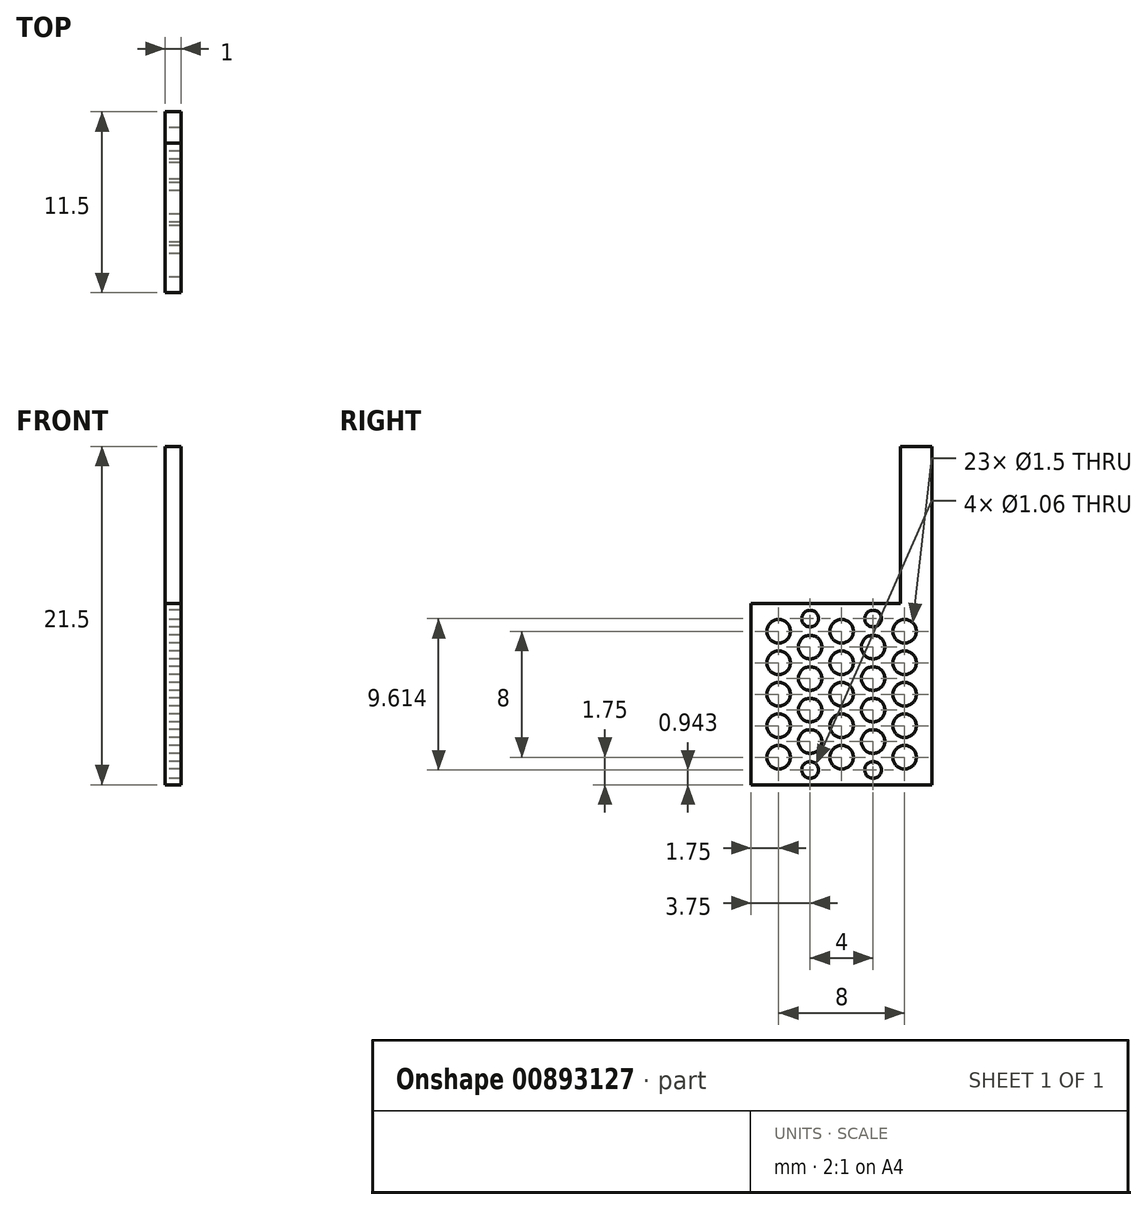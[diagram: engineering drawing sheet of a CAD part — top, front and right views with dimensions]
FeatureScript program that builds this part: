
annotation { "Feature Type Name" : "Feature", "Feature Type Description" : "" }
export const myFeature = defineFeature(function(context is Context, id is Id, definition is map)
    precondition{}
    {
        {
            var Q0;
            Q0=qCreatedBy(makeId("Right.planeOp"),FACE);
            var sketch = newSketch(context, id + "F0", { "sketchPlane" : qUnion([Q0])});
            skLineSegment(sketch, "E0.bottom", {"start": v(0, 0) * mm, "end": v(8.38, 0) * mm});
            skLineSegment(sketch, "E0.top", {"start": v(0, -11.5) * mm, "end": v(11.5, -11.5) * mm});
            skLineSegment(sketch, "E0.left", {"start": v(0, 0) * mm, "end": v(0, -11.5) * mm});
            skLineSegment(sketch, "E1", {"start": v(11.5, 0) * mm, "end": v(11.5, -11.5) * mm});
            skLineSegment(sketch, "E2", {"start": v(10.38, 10) * mm, "end": v(9.5, 10) * mm});
            skLineSegment(sketch, "E3.trimOffspring", {"start": v(10.38, 0) * mm, "end": v(11.5, 0) * mm});
            skCircle(sketch, "E4", {"center": v(1.75, -5.75) * mm, "radius": 0.75 * mm});
            skCircle(sketch, "E5.MirrorC", {"center": v(1.75, -1.75) * mm, "radius": 0.75 * mm});
            skCircle(sketch, "E6.MirrorC", {"center": v(1.75, -3.75) * mm, "radius": 0.75 * mm});
            skCircle(sketch, "E7.MirrorC", {"center": v(1.75, -9.75) * mm, "radius": 0.75 * mm});
            skCircle(sketch, "E8.MirrorC", {"center": v(1.75, -7.75) * mm, "radius": 0.75 * mm});
            skCircle(sketch, "E9", {"center": v(3.75, -2.75) * mm, "radius": 0.75 * mm});
            skCircle(sketch, "E10", {"center": v(3.75, -10.56) * mm, "radius": 0.53 * mm});
            skCircle(sketch, "E11.MirrorC", {"center": v(5.75, -1.75) * mm, "radius": 0.75 * mm});
            skCircle(sketch, "E12.MirrorC", {"center": v(5.75, -3.75) * mm, "radius": 0.75 * mm});
            skCircle(sketch, "E13.MirrorC", {"center": v(5.75, -5.75) * mm, "radius": 0.75 * mm});
            skCircle(sketch, "E14.MirrorC", {"center": v(5.75, -7.75) * mm, "radius": 0.75 * mm});
            skCircle(sketch, "E15.MirrorC", {"center": v(5.75, -9.75) * mm, "radius": 0.75 * mm});
            skCircle(sketch, "E16.MirrorC", {"center": v(7.75, -2.75) * mm, "radius": 0.75 * mm});
            skCircle(sketch, "E17.MirrorC", {"center": v(9.75, -1.75) * mm, "radius": 0.75 * mm});
            skCircle(sketch, "E18.MirrorC", {"center": v(9.75, -3.75) * mm, "radius": 0.75 * mm});
            skCircle(sketch, "E19.MirrorC", {"center": v(9.75, -5.75) * mm, "radius": 0.75 * mm});
            skCircle(sketch, "E20.MirrorC", {"center": v(9.75, -7.75) * mm, "radius": 0.75 * mm});
            skCircle(sketch, "E21.MirrorC", {"center": v(9.75, -9.75) * mm, "radius": 0.75 * mm});
            skCircle(sketch, "E22", {"center": v(7.75, -10.56) * mm, "radius": 0.53 * mm});
            skCircle(sketch, "E23", {"center": v(3.75, -0.94) * mm, "radius": 0.53 * mm});
            skCircle(sketch, "E24", {"center": v(7.75, -0.94) * mm, "radius": 0.53 * mm});
            skCircle(sketch, "E25", {"center": v(3.75, -4.75) * mm, "radius": 0.75 * mm});
            skCircle(sketch, "E26", {"center": v(3.75, -6.75) * mm, "radius": 0.75 * mm});
            skCircle(sketch, "E27", {"center": v(3.75, -8.75) * mm, "radius": 0.75 * mm});
            skCircle(sketch, "E28.MirrorC", {"center": v(7.75, -4.75) * mm, "radius": 0.75 * mm});
            skCircle(sketch, "E29.MirrorC", {"center": v(7.75, -6.75) * mm, "radius": 0.75 * mm});
            skCircle(sketch, "E30.MirrorC", {"center": v(7.75, -8.75) * mm, "radius": 0.75 * mm});
            skLineSegment(sketch, "E31", {"start": v(11.5, 0) * mm, "end": v(11.5, 10) * mm});
            skLineSegment(sketch, "E32", {"start": v(11.5, 10) * mm, "end": v(10.38, 10) * mm});
            skLineSegment(sketch, "E33.0", {"start": v(9.5, 10) * mm, "end": v(9.5, 0) * mm});
            skLineSegment(sketch, "E34", {"start": v(10.38, 0) * mm, "end": v(8.38, 0) * mm});
            skLineSegment(sketch, "E35", {"start": v(9.5, 0) * mm, "end": v(11.24, 0) * mm});
            skSolve(sketch);
        }
        {
            var Q0;
            Q0=makeQuery(id+"F0.imprint","IMPRINT",FACE,{"disambiguationData":[TD([[makeQuery(id+"F0.imprint","IMPRINT",EDGE,{"derivedFrom":sQuery(id+"F0.wireOp",EDGE,"E0.bottom")}),-1.0]])]});
            var Q1;
            Q1=makeQuery(id+"F0.imprint","IMPRINT",FACE,{"disambiguationData":[TD([[makeQuery(id+"F0.imprint","IMPRINT",EDGE,{"derivedFrom":sQuery(id+"F0.wireOp",EDGE,"r65wuaeR-pUGk-UfhY-v5oq-7bkjaNJfQmKm.bottom")}),-1.0]])]});
            var Q2;
            Q2=makeQuery(id+"F0.imprint","IMPRINT",FACE,{"disambiguationData":[TD([[makeQuery(id+"F0.imprint","IMPRINT",EDGE,{"derivedFrom":sQuery(id+"F0.wireOp",EDGE,"n5EaUuf3-CoM6-EQkv-XzT1-ydr3onYee1LO.bottom")}),1.0]])]});
            var Q3;
            Q3=makeQuery(id+"F0.imprint","IMPRINT",FACE,{"disambiguationData":[TD([[makeQuery(id+"F0.imprint","IMPRINT",EDGE,{"derivedFrom":sQuery(id+"F0.wireOp",EDGE,"2NUbogVr-x7fL-9LVX-WR3f-6RiyyzUn8nbi.bottom")}),-1.0]])]});
            var Q4;
            Q4=makeQuery(id+"F0.imprint","IMPRINT",FACE,{"disambiguationData":[TD([[makeQuery(id+"F0.imprint","IMPRINT",EDGE,{"derivedFrom":sQuery(id+"F0.wireOp",EDGE,"E2")}),1.0]])]});
            extrude(context, id + "F1", {"entities" : qUnion([Q0, Q1, Q2, Q3, Q4]), "depth" : 1 * mm, "offsetDistance" : 25 * mm});
        }
    });
